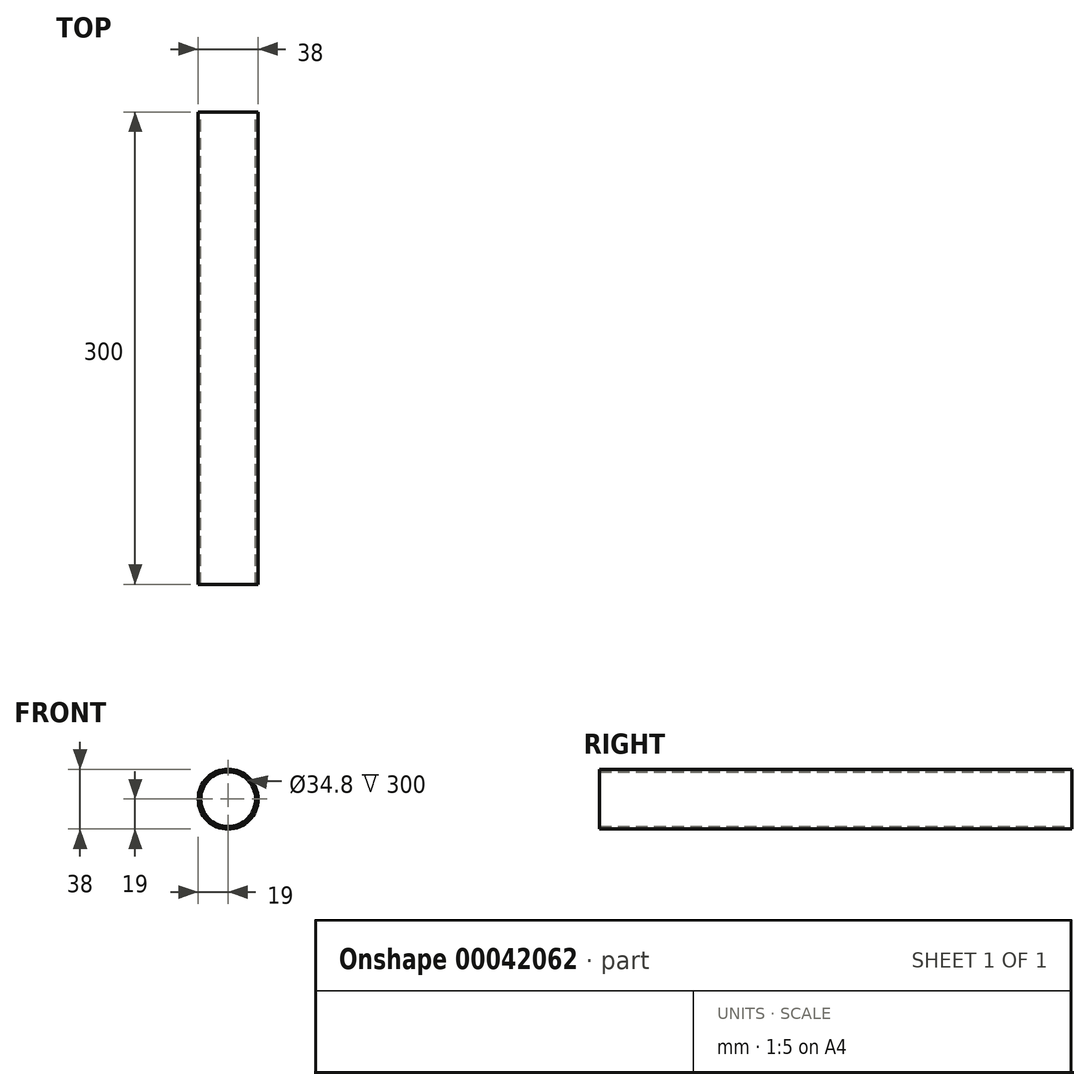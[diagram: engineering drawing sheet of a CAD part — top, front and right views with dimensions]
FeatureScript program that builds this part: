
annotation { "Feature Type Name" : "Feature", "Feature Type Description" : "" }
export const myFeature = defineFeature(function(context is Context, id is Id, definition is map)
    precondition{}
    {
        {
            var Q0;
            Q0=qCreatedBy(makeId("Front.planeOp"),FACE);
            var sketch = newSketch(context, id + "F0", { "sketchPlane" : qUnion([Q0])});
            skCircle(sketch, "E0", {"center": v(0, 0) * mm, "radius": 19 * mm});
            skCircle(sketch, "E1.0", {"center": v(0, 0) * mm, "radius": 17.4 * mm});
            skSolve(sketch);
        }
        {
            var Q0;
            Q0=makeQuery(id+"F0.imprint","IMPRINT",FACE,{"disambiguationData":[TD([[makeQuery(id+"F0.imprint","IMPRINT",EDGE,{"derivedFrom":sQuery(id+"F0.wireOp",EDGE,"E0")}),1.0]])]});
            extrude(context, id + "F1", {"entities" : qUnion([Q0]), "depth" : 300 * mm});
        }
    });
